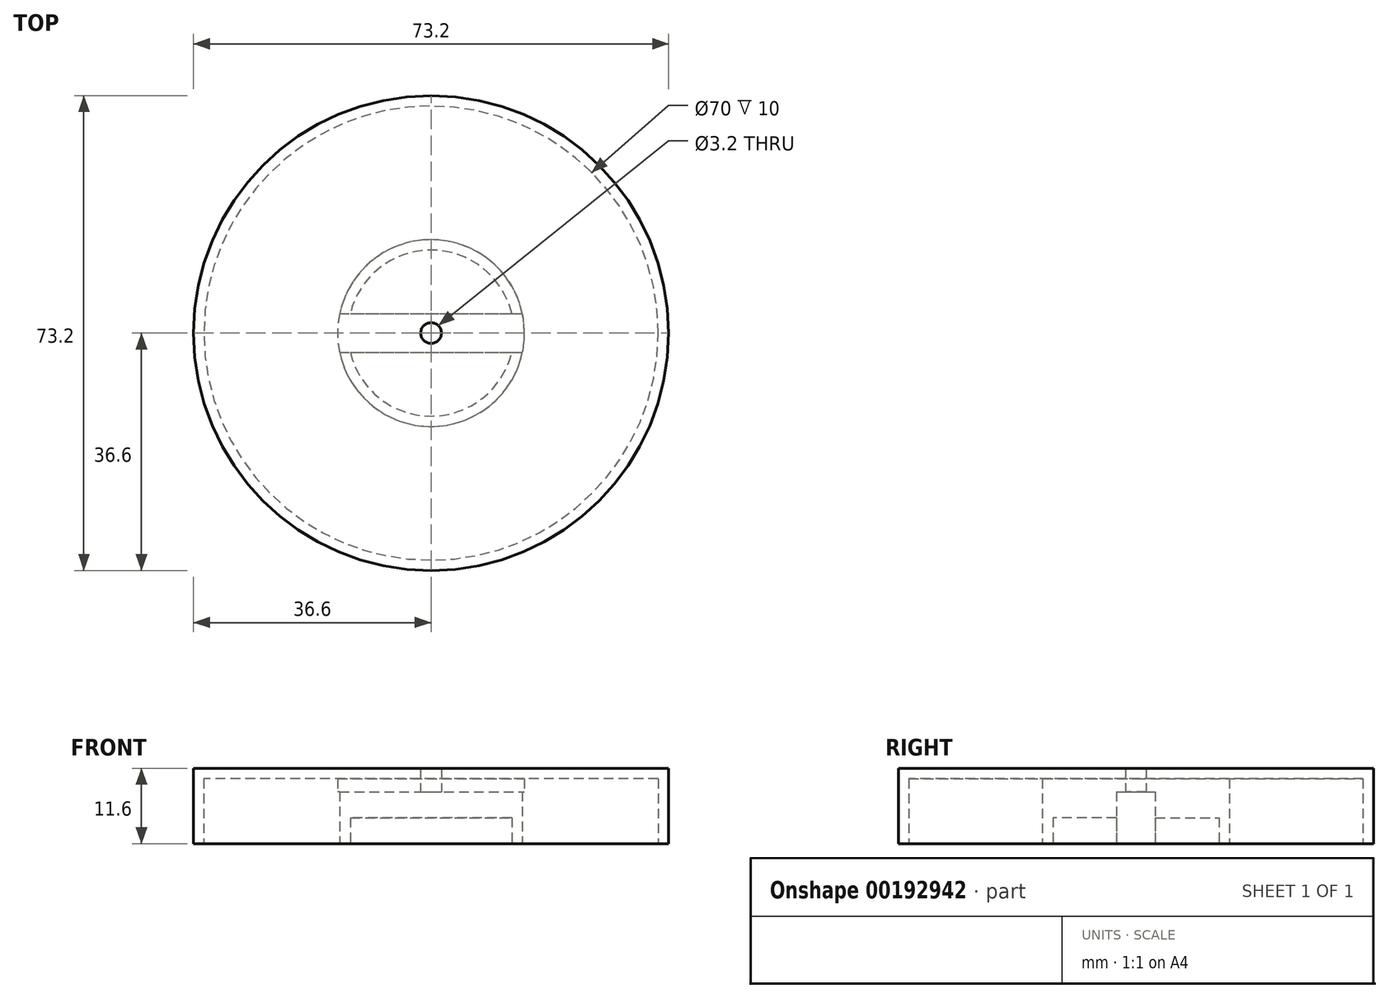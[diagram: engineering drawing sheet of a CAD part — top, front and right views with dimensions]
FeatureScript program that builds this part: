
annotation { "Feature Type Name" : "Feature", "Feature Type Description" : "" }
export const myFeature = defineFeature(function(context is Context, id is Id, definition is map)
    precondition{}
    {
        {
            var Q0;
            Q0=qCreatedBy(makeId("Top.planeOp"),FACE);
            var sketch = newSketch(context, id + "F0", { "sketchPlane" : qUnion([Q0])});
            skCircle(sketch, "E0", {"center": v(0, 0) * mm, "radius": 12.8 * mm});
            skCircle(sketch, "E1", {"center": v(0, 0) * mm, "radius": 14.4 * mm});
            skCircle(sketch, "E2", {"center": v(0, 0) * mm, "radius": 35 * mm});
            skCircle(sketch, "E3", {"center": v(0, 0) * mm, "radius": 36.6 * mm});
            skSolve(sketch);
        }
        {
            var Q0;
            Q0 = qSketchRegion(id + "F0", true);
            var Q1;
            Q1=makeQuery(id+"F0.imprint","IMPRINT",FACE,{"disambiguationData":[TD([[makeQuery(id+"F0.imprint","IMPRINT",EDGE,{"derivedFrom":sQuery(id+"F0.wireOp",EDGE,"E0")}),-1.0]])]});
            extrude(context, id + "F1", {"entities" : qUnion([Q0, Q1]), "depth" : 10 * mm});
        }
        {
            var Q0;
            Q0=makeQuery(id+"F1.opExtrude","CAP_FACE",FACE,{"disambiguationData":[OSD([sQuery(id+"F0.wireOp",EDGE,"E0"),sQuery(id+"F0.wireOp",EDGE,"E1")])],"isStart":false});
            var sketch = newSketch(context, id + "F2", { "sketchPlane" : qUnion([Q0])});
            skCircle(sketch, "E4.0", {"center": v(0, 0) * mm, "radius": 36.6 * mm});
            skSolve(sketch);
        }
        {
            var Q0;
            Q0 = qSketchRegion(id + "F2", true);
            extrude(context, id + "F3", {"entities" : qUnion([Q0]), "operationType" : NewBodyOperationType.ADD, "depth" : 1.6 * mm});
        }
        {
            var Q0;
            Q0=makeQuery(id+"F3.boolean.opBoolean","SPLIT",FACE,{"disambiguationData":[TD([makeQuery(id+"F1.opExtrude","SWEPT_FACE",FACE,{"disambiguationData":[OSD([sQuery(id+"F0.wireOp",EDGE,"E0")])]})])],"derivedFrom":makeQuery(id+"F3.opExtrude","CAP_FACE",FACE,{"disambiguationData":[OSD([sQuery(id+"F2.wireOp",EDGE,"E4.0")])],"isStart":true})});
            var sketch = newSketch(context, id + "F4", { "sketchPlane" : qUnion([Q0])});
            skCircle(sketch, "E5.0.0", {"center": v(0, 0) * mm, "radius": 12.8 * mm});
            skSolve(sketch);
        }
        {
            var Q0;
            Q0 = qSketchRegion(id + "F4", true);
            extrude(context, id + "F5", {"entities" : qUnion([Q0]), "operationType" : NewBodyOperationType.ADD, "depth" : 6 * mm});
        }
        {
            var Q0;
            Q0=makeQuery(id+"F1.opExtrude","CAP_FACE",FACE,{"disambiguationData":[OSD([sQuery(id+"F0.wireOp",EDGE,"E0"),sQuery(id+"F0.wireOp",EDGE,"E1")])],"isStart":true});
            var sketch = newSketch(context, id + "F6", { "sketchPlane" : qUnion([Q0])});
            skLineSegment(sketch, "E6.bottom", {"start": v(-20.45, 3) * mm, "end": v(20.45, 3) * mm});
            skLineSegment(sketch, "E6.top", {"start": v(-20.45, -3) * mm, "end": v(20.45, -3) * mm});
            skLineSegment(sketch, "E6.left", {"start": v(-20.45, 3) * mm, "end": v(-20.45, -3) * mm});
            skLineSegment(sketch, "E6.right", {"start": v(20.45, 3) * mm, "end": v(20.45, -3) * mm});
            skPoint(sketch, "E6.middle", {"position": v(0, 0) * mm});
            skSolve(sketch);
        }
        {
            var Q0;
            Q0 = qSketchRegion(id + "F6", true);
            extrude(context, id + "F7", {"entities" : qUnion([Q0]), "operationType" : NewBodyOperationType.REMOVE, "oppositeDirection" : true, "depth" : 8 * mm});
        }
        {
            var Q0;
            Q0=makeQuery(id+"F7.boolean.opBoolean","COPY",FACE,{"derivedFrom":makeQuery(id+"F7.opExtrude","CAP_FACE",FACE,{"disambiguationData":[OSD([sQuery(id+"F6.wireOp",EDGE,"E6.bottom"),sQuery(id+"F6.wireOp",EDGE,"E6.top"),sQuery(id+"F6.wireOp",EDGE,"E6.left"),sQuery(id+"F6.wireOp",EDGE,"E6.right")])],"isStart":false})});
            var sketch = newSketch(context, id + "F8", { "sketchPlane" : qUnion([Q0])});
            skCircle(sketch, "E7", {"center": v(0, 0) * mm, "radius": 1.6 * mm});
            skSolve(sketch);
        }
        {
            var Q0;
            Q0 = qSketchRegion(id + "F8", true);
            extrude(context, id + "F9", {"entities" : qUnion([Q0]), "operationType" : NewBodyOperationType.REMOVE, "oppositeDirection" : true, "depth" : 25 * mm});
        }
    });
